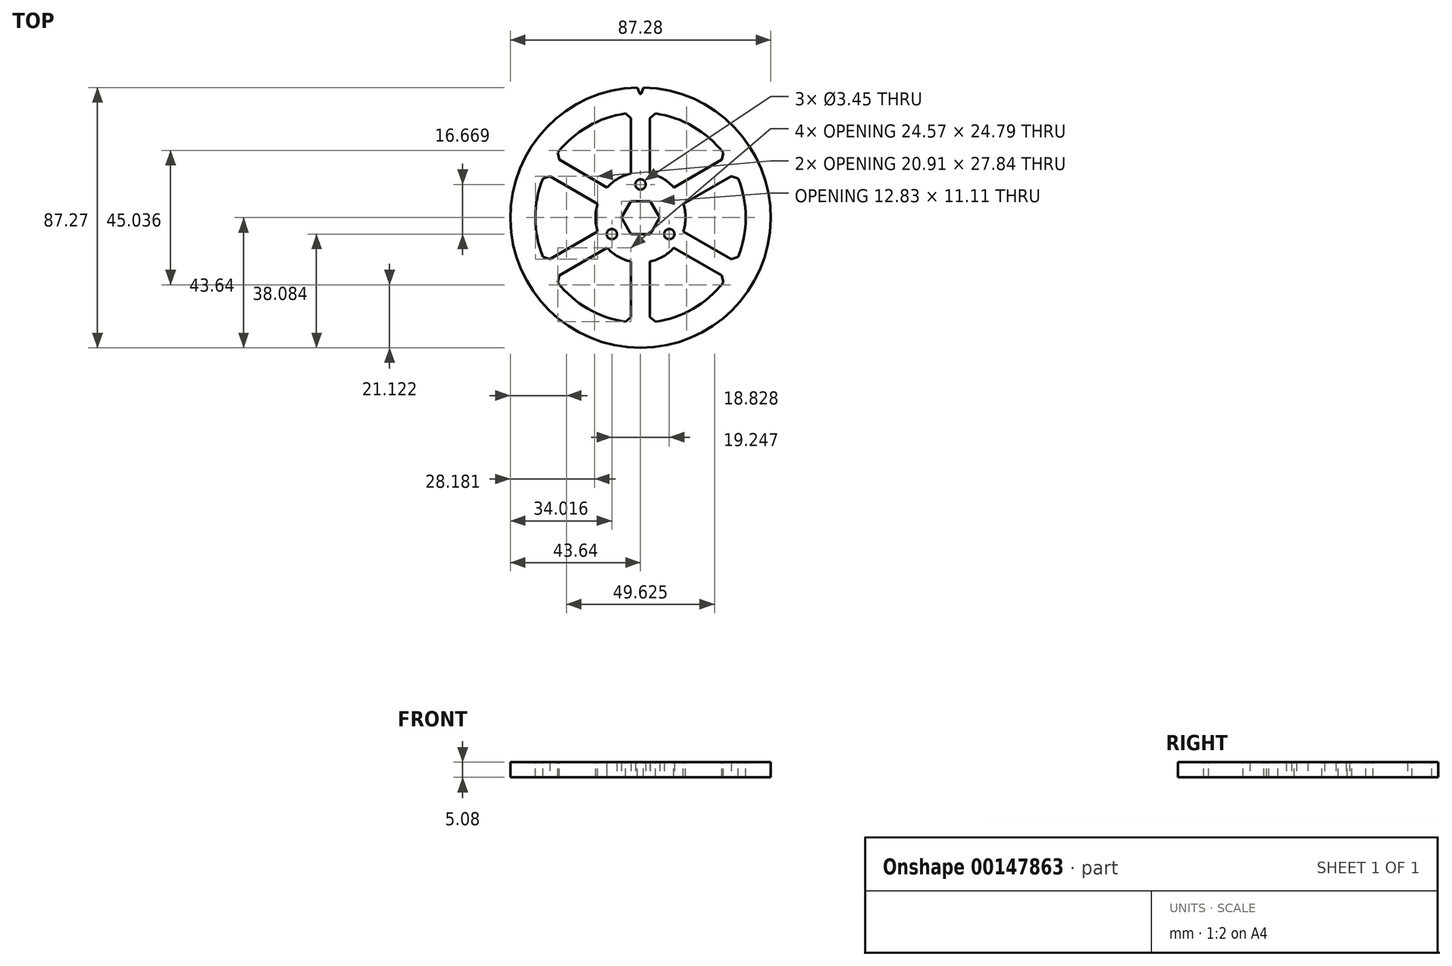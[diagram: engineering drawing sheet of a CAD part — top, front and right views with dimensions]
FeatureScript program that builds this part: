
annotation { "Feature Type Name" : "Feature", "Feature Type Description" : "" }
export const myFeature = defineFeature(function(context is Context, id is Id, definition is map)
    precondition{}
    {
        {
            var Q0;
            Q0=qCreatedBy(makeId("Top.planeOp"),FACE);
            var sketch = newSketch(context, id + "F0", { "sketchPlane" : qUnion([Q0])});
            skPoint(sketch, "E0.middle", {"position": v(0, 0) * mm});
            skCircle(sketch, "E1", {"center": v(0, 0) * mm, "radius": 43.64 * mm});
            skCircle(sketch, "E2.cCircle", {"center": v(0, 0) * mm, "radius": 5.56 * mm, "construction": true});
            skLineSegment(sketch, "E2.0", {"start": v(3.2, -5.56) * mm, "end": v(-3.2, -5.56) * mm});
            skLineSegment(sketch, "E2.1", {"start": v(-3.2, -5.56) * mm, "end": v(-6.42, 0) * mm});
            skLineSegment(sketch, "E2.2", {"start": v(-6.42, 0) * mm, "end": v(-3.2, 5.56) * mm});
            skLineSegment(sketch, "E2.3", {"start": v(-3.2, 5.56) * mm, "end": v(3.2, 5.56) * mm});
            skLineSegment(sketch, "E2.4", {"start": v(3.2, 5.56) * mm, "end": v(6.42, 0) * mm});
            skLineSegment(sketch, "E2.5", {"start": v(6.42, 0) * mm, "end": v(3.2, -5.56) * mm});
            skPoint(sketch, "E2.0.midPoint", {"position": v(0, -5.56) * mm});
            skLineSegment(sketch, "E3.0", {"start": v(9.62, -5.56) * mm, "end": v(-9.62, -5.56) * mm, "construction": true});
            skLineSegment(sketch, "E3.1", {"start": v(-9.62, -5.56) * mm, "end": v(0, 11.11) * mm, "construction": true});
            skLineSegment(sketch, "E3.2", {"start": v(0, 11.11) * mm, "end": v(9.62, -5.56) * mm, "construction": true});
            skCircle(sketch, "E4", {"center": v(0, 0) * mm, "radius": 7.14 * mm, "construction": true});
            skCircle(sketch, "E5", {"center": v(0, 11.11) * mm, "radius": 3.97 * mm, "construction": true});
            skCircle(sketch, "E6", {"center": v(0, 11.11) * mm, "radius": 1.73 * mm});
            skCircle(sketch, "E7", {"center": v(9.62, -5.56) * mm, "radius": 1.73 * mm});
            skCircle(sketch, "E8", {"center": v(-9.62, -5.56) * mm, "radius": 1.73 * mm});
            skSolve(sketch);
        }
        {
            var Q0;
            Q0=makeQuery(id+"F0.imprint","IMPRINT",FACE,{"disambiguationData":[TD([[makeQuery(id+"F0.imprint","IMPRINT",EDGE,{"derivedFrom":sQuery(id+"F0.wireOp",EDGE,"E0.left")}),1.0]])]});
            var Q1;
            Q1=makeQuery(id+"F0.imprint","IMPRINT",FACE,{"disambiguationData":[TD([[makeQuery(id+"F0.imprint","IMPRINT",EDGE,{"derivedFrom":sQuery(id+"F0.wireOp",EDGE,"E1")}),1.0]])]});
            extrude(context, id + "F1", {"entities" : qUnion([Q0, Q1]), "depth" : 5.08 * mm});
        }
        {
            var Q0;
            Q0=makeQuery(id+"F1.opExtrude","CAP_FACE",FACE,{"disambiguationData":[OSD([sQuery(id+"F0.wireOp",EDGE,"E0.left"),sQuery(id+"F0.wireOp",EDGE,"E0.right"),sQuery(id+"F0.wireOp",EDGE,"ScfBMfkV-s1yN-Ls9R-SGr5-fEyGpD6zak8e"),sQuery(id+"F0.wireOp",EDGE,"xnxmVwjl-FvSF-m7sj-be2U-u85gZZGoORGZ"),sQuery(id+"F0.wireOp",EDGE,"E1")])],"isStart":false});
            var sketch = newSketch(context, id + "F2", { "sketchPlane" : qUnion([Q0])});
            skLineSegment(sketch, "E9", {"start": v(0, 0) * mm, "end": v(0, 43.64) * mm, "construction": true});
            skLineSegment(sketch, "E10", {"start": v(0, 0) * mm, "end": v(0.67, 43.63) * mm, "construction": true});
            skArc(sketch, "E11", {"start": v(1.03, 43.63) * mm, "mid": v(0, 43.64) * mm, "end": v(-1.03, 43.63) * mm});
            skLineSegment(sketch, "E12", {"start": v(-1.03, 43.63) * mm, "end": v(-0.28, 41.67) * mm});
            skLineSegment(sketch, "E13", {"start": v(1.03, 43.63) * mm, "end": v(0.28, 41.67) * mm});
            skPoint(sketch, "E14", {"position": v(0.65, 42.65) * mm});
            skArc(sketch, "E15", {"start": v(-0.28, 41.67) * mm, "mid": v(0, 41.48) * mm, "end": v(0.28, 41.67) * mm});
            skSolve(sketch);
        }
        {
            var Q0;
            Q0=qSketchRegion(id+"F2",true);
            var Q1;
            Q1=makeQuery(id+"F1.opExtrude","CAP_FACE",FACE,{"disambiguationData":[OSD([sQuery(id+"F0.wireOp",EDGE,"E0.left"),sQuery(id+"F0.wireOp",EDGE,"E0.right"),sQuery(id+"F0.wireOp",EDGE,"ScfBMfkV-s1yN-Ls9R-SGr5-fEyGpD6zak8e"),sQuery(id+"F0.wireOp",EDGE,"xnxmVwjl-FvSF-m7sj-be2U-u85gZZGoORGZ"),sQuery(id+"F0.wireOp",EDGE,"E1")])],"isStart":true});
            extrude(context, id + "F3", {"entities" : qUnion([Q0]), "operationType" : NewBodyOperationType.REMOVE, "endBound" : BoundingType.UP_TO_SURFACE, "oppositeDirection" : true, "endBoundEntityFace" : qUnion([Q1]), "depth" : 25.4 * mm});
        }
        {
            var Q0;
            Q0=makeQuery(id+"F1.opExtrude","CAP_FACE",FACE,{"disambiguationData":[OSD([sQuery(id+"F0.wireOp",EDGE,"E1"),sQuery(id+"F0.wireOp",EDGE,"E2.0"),sQuery(id+"F0.wireOp",EDGE,"E2.1"),sQuery(id+"F0.wireOp",EDGE,"E2.2"),sQuery(id+"F0.wireOp",EDGE,"E2.3"),sQuery(id+"F0.wireOp",EDGE,"E2.4"),sQuery(id+"F0.wireOp",EDGE,"E2.5"),sQuery(id+"F0.wireOp",EDGE,"E6"),sQuery(id+"F0.wireOp",EDGE,"E7"),sQuery(id+"F0.wireOp",EDGE,"E8")])],"isStart":false});
            var sketch = newSketch(context, id + "F4", { "sketchPlane" : qUnion([Q0])});
            skLineSegment(sketch, "E16", {"start": v(3.18, 14.74) * mm, "end": v(3.17, 35.13) * mm});
            skArc(sketch, "E17", {"start": v(11.18, 10.12) * mm, "mid": v(7.54, 13.06) * mm, "end": v(3.18, 14.74) * mm});
            skArc(sketch, "E18", {"start": v(28.83, 20.31) * mm, "mid": v(17.63, 30.54) * mm, "end": v(3.18, 35.13) * mm});
            skLineSegment(sketch, "E19", {"start": v(0, 41.48) * mm, "end": v(0, 35.13) * mm, "construction": true});
            skLineSegment(sketch, "E20", {"start": v(11.18, 10.12) * mm, "end": v(28.83, 20.31) * mm});
            skLineSegment(sketch, "E21", {"start": v(0, 0) * mm, "end": v(0, 14.74) * mm, "construction": true});
            skLineSegment(sketch, "E22.bottom", {"start": v(0, 14.74) * mm, "end": v(3.18, 14.74) * mm, "construction": true});
            skLineSegment(sketch, "E22.top", {"start": v(0, 35.13) * mm, "end": v(3.17, 35.13) * mm, "construction": true});
            skLineSegment(sketch, "E23", {"start": v(11.18, 10.12) * mm, "end": v(12.77, 7.37) * mm, "construction": true});
            skLineSegment(sketch, "E24", {"start": v(12.77, 7.37) * mm, "end": v(0, 0) * mm, "construction": true});
            skSolve(sketch);
        }
        {
            var Q0;
            Q0=qSketchRegion(id+"F4",true);
            var Q1;
            Q1=makeQuery(id+"F1.opExtrude","CAP_FACE",FACE,{"disambiguationData":[OSD([sQuery(id+"F0.wireOp",EDGE,"E1"),sQuery(id+"F0.wireOp",EDGE,"E2.0"),sQuery(id+"F0.wireOp",EDGE,"E2.1"),sQuery(id+"F0.wireOp",EDGE,"E2.2"),sQuery(id+"F0.wireOp",EDGE,"E2.3"),sQuery(id+"F0.wireOp",EDGE,"E2.4"),sQuery(id+"F0.wireOp",EDGE,"E2.5"),sQuery(id+"F0.wireOp",EDGE,"E6"),sQuery(id+"F0.wireOp",EDGE,"E7"),sQuery(id+"F0.wireOp",EDGE,"E8")])],"isStart":true});
            extrude(context, id + "F5", {"entities" : qUnion([Q0]), "operationType" : NewBodyOperationType.REMOVE, "endBound" : BoundingType.UP_TO_SURFACE, "oppositeDirection" : true, "endBoundEntityFace" : qUnion([Q1]), "depth" : 25.4 * mm});
        }
        {
            var Q0;
            Q0=makeQuery(id+"F7.3.F5.boolean.opBoolean","COPY",EDGE,{"derivedFrom":makeQuery(id+"F7.3.F5.opExtrude","SWEPT_EDGE",EDGE,{"disambiguationData":[OSD([sQuery(id+"F4.wireOp",EDGE,"E16"),sQuery(id+"F4.wireOp",EDGE,"E18")])]})});
            var Q1;
            Q1=makeQuery(id+"F7.3.F5.boolean.opBoolean","COPY",EDGE,{"derivedFrom":makeQuery(id+"F7.3.F5.opExtrude","SWEPT_EDGE",EDGE,{"disambiguationData":[OSD([sQuery(id+"F4.wireOp",EDGE,"E16"),sQuery(id+"F4.wireOp",EDGE,"E17")])]})});
            var Q2;
            Q2=makeQuery(id+"F7.3.F5.boolean.opBoolean","COPY",EDGE,{"derivedFrom":makeQuery(id+"F7.3.F5.opExtrude","SWEPT_EDGE",EDGE,{"disambiguationData":[OSD([sQuery(id+"F4.wireOp",EDGE,"E17"),sQuery(id+"F4.wireOp",EDGE,"E20")])]})});
            var Q3;
            Q3=makeQuery(id+"F7.3.F5.boolean.opBoolean","COPY",EDGE,{"derivedFrom":makeQuery(id+"F7.3.F5.opExtrude","SWEPT_EDGE",EDGE,{"disambiguationData":[OSD([sQuery(id+"F4.wireOp",EDGE,"E18"),sQuery(id+"F4.wireOp",EDGE,"E20")])]})});
            var Q4;
            Q4=makeQuery(id+"F5.boolean.opBoolean","COPY",EDGE,{"derivedFrom":makeQuery(id+"F5.opExtrude","SWEPT_EDGE",EDGE,{"disambiguationData":[OSD([sQuery(id+"F4.wireOp",EDGE,"E16"),sQuery(id+"F4.wireOp",EDGE,"E18")])]})});
            var Q5;
            Q5=makeQuery(id+"F5.boolean.opBoolean","COPY",EDGE,{"derivedFrom":makeQuery(id+"F5.opExtrude","SWEPT_EDGE",EDGE,{"disambiguationData":[OSD([sQuery(id+"F4.wireOp",EDGE,"E18"),sQuery(id+"F4.wireOp",EDGE,"E20")])]})});
            chamfer(context, id + "F6", {"entities" : qUnion([Q0, Q1, Q2, Q3, Q4, Q5]), "width" : 1.59 * mm, "tangentPropagation" : true});
        }
        {
            var Q0;
            Q0=makeQuery(id+"F6.opChamfer","BLEND_FACE",FACE,{"disambiguationData":[OSD([sQuery(id+"F4.wireOp",EDGE,"E18"),sQuery(id+"F4.wireOp",EDGE,"E20")])]});
            var Q1;
            Q1=makeQuery(id+"F5.boolean.opBoolean","COPY",FACE,{"derivedFrom":makeQuery(id+"F5.opExtrude","SWEPT_FACE",FACE,{"disambiguationData":[OSD([sQuery(id+"F4.wireOp",EDGE,"E20")])]})});
            var Q2;
            Q2=makeQuery(id+"F6.opChamfer","BLEND_FACE",FACE,{"disambiguationData":[OSD([sQuery(id+"F4.wireOp",EDGE,"E17"),sQuery(id+"F4.wireOp",EDGE,"E20")])]});
            var Q3;
            Q3=makeQuery(id+"F5.boolean.opBoolean","COPY",FACE,{"derivedFrom":makeQuery(id+"F5.opExtrude","SWEPT_FACE",FACE,{"disambiguationData":[OSD([sQuery(id+"F4.wireOp",EDGE,"E17")])]})});
            var Q4;
            Q4=makeQuery(id+"F6.opChamfer","BLEND_FACE",FACE,{"disambiguationData":[OSD([sQuery(id+"F4.wireOp",EDGE,"E16"),sQuery(id+"F4.wireOp",EDGE,"E17")])]});
            var Q5;
            Q5=makeQuery(id+"F5.boolean.opBoolean","COPY",FACE,{"derivedFrom":makeQuery(id+"F5.opExtrude","SWEPT_FACE",FACE,{"disambiguationData":[OSD([sQuery(id+"F4.wireOp",EDGE,"E16")])]})});
            var Q6;
            Q6=makeQuery(id+"F6.opChamfer","BLEND_FACE",FACE,{"disambiguationData":[OSD([sQuery(id+"F4.wireOp",EDGE,"E16"),sQuery(id+"F4.wireOp",EDGE,"E18")])]});
            var Q7;
            Q7=makeQuery(id+"F5.boolean.opBoolean","COPY",FACE,{"derivedFrom":makeQuery(id+"F5.opExtrude","SWEPT_FACE",FACE,{"disambiguationData":[OSD([sQuery(id+"F4.wireOp",EDGE,"E18")])]})});
            var Q8;
            Q8=makeQuery(id+"F5.boolean.opBoolean","COPY",FACE,{"derivedFrom":makeQuery(id+"F5.opExtrude","SWEPT_FACE",FACE,{"disambiguationData":[OSD([sQuery(id+"F4.wireOp",EDGE,"E18")])]})});
            circularPattern(context, id + "F7", {"patternType" : PatternType.FACE, "faces" : qUnion([Q0, Q1, Q2, Q3, Q4, Q5, Q6, Q7]), "axis" : qUnion([Q8]), "angle" : 60 * degree, "instanceCount" : 6});
        }
    });
